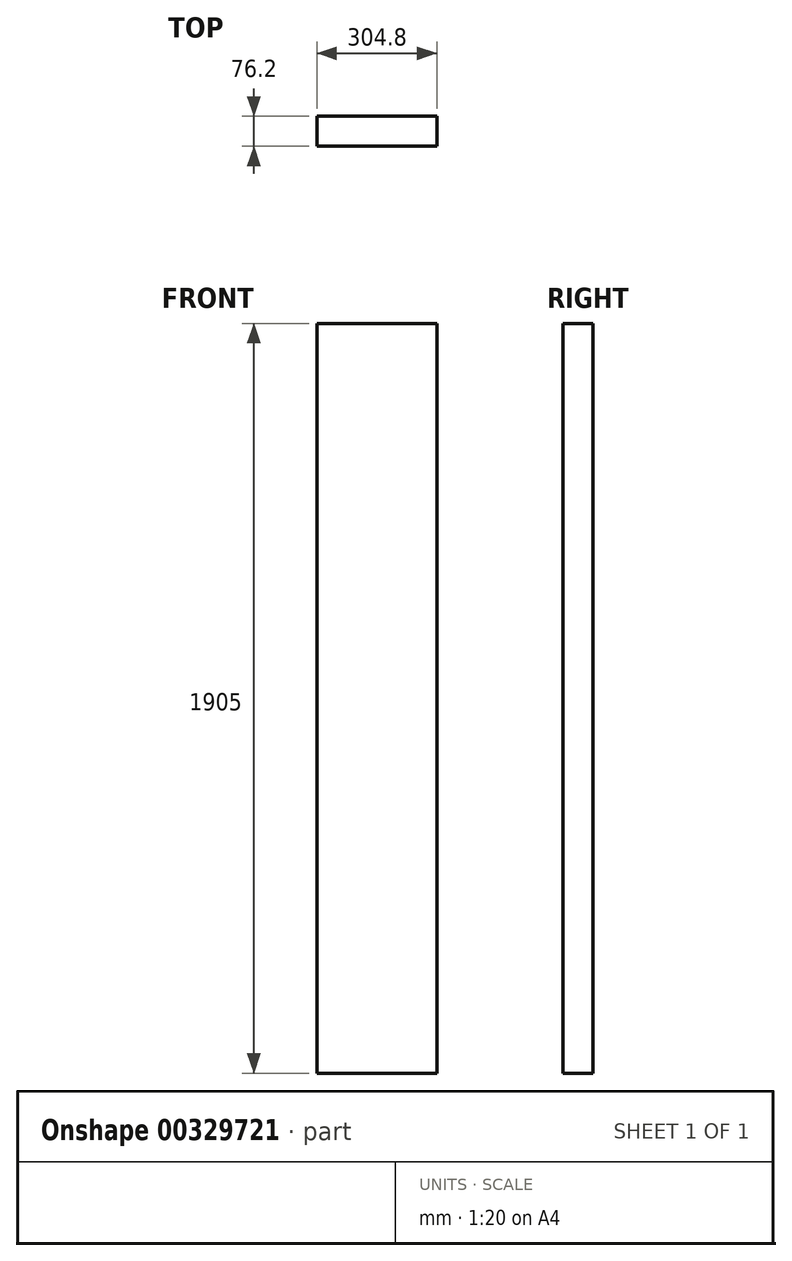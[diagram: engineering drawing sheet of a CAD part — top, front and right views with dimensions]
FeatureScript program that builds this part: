
annotation { "Feature Type Name" : "Feature", "Feature Type Description" : "" }
export const myFeature = defineFeature(function(context is Context, id is Id, definition is map)
    precondition{}
    {
        {
            var Q0;
            Q0=qCreatedBy(makeId("Front.planeOp"),FACE);
            var sketch = newSketch(context, id + "F0", { "sketchPlane" : qUnion([Q0])});
            skLineSegment(sketch, "E0.bottom", {"start": v(-152.4, 952.5) * mm, "end": v(152.4, 952.5) * mm});
            skLineSegment(sketch, "E0.top", {"start": v(-152.4, -952.5) * mm, "end": v(152.4, -952.5) * mm});
            skLineSegment(sketch, "E0.left", {"start": v(-152.4, 952.5) * mm, "end": v(-152.4, -952.5) * mm});
            skLineSegment(sketch, "E0.right", {"start": v(152.4, 952.5) * mm, "end": v(152.4, -952.5) * mm});
            skPoint(sketch, "E0.middle", {"position": v(0, 0) * mm});
            skSolve(sketch);
        }
        {
            var Q0;
            Q0=makeQuery(id+"F0.imprint","IMPRINT",FACE,{"disambiguationData":[TD([[makeQuery(id+"F0.imprint","IMPRINT",EDGE,{"derivedFrom":sQuery(id+"F0.wireOp",EDGE,"E0.bottom")}),-1.0]])]});
            extrude(context, id + "F1", {"entities" : qUnion([Q0]), "endBound" : BoundingType.SYMMETRIC, "depth" : 76.2 * mm});
        }
    });
